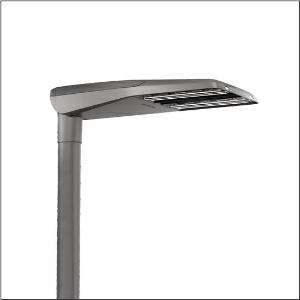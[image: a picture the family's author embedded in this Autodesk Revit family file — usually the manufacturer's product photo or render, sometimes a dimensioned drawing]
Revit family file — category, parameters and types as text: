
# Revit family: streetlight_sl_11_iq_midi___st1_2p1_0_5xc3g41f08me_0c33
name_source: partatom
category: Lighting Fixtures
units: mm (PartAtom-declared; Revit-internal decimal feet)

## family parameters
Cut with Voids When Loaded = No
Host = Face
Light Source = No
Part Type = Normal
Room Calculation Point = No
Round Connector Dimension = Use Diameter
Shared = No

## types (1)
- --- (1 x LED, 18520 lm, 124.7 W, 4000K)
    Apparent Load = 125 VA
    CIE Flux Codes = 31 68 95 100 100
    Color Rendering = 70
    Color Temperature = 4000K
    Default Elevation = 1800 mm
    Description = Streetlight SL 11 iQ midi, mast luminaire, primary light control with 3 zone facetted reflector, of plastic, silver coated, highly specular, primary optical cover: cover, of PMMA, transparent, light distribution: ST1.2P1.0, light emission: direct distribution, primary light characteristic: asymmetric, installation type: post-top, side-entry, LED, High Power LED, rated luminous flux: 18.520lm, luminous efficacy: 149lm/W, light colour: 740, colour temperature: 4000K, control: Street-Remote, optimised constant luminous flux control (CLO 2.0), Auto-Match, Desk-Remote (wireless, voltage-free reading and setting of iQ features in the workshop via application-optimized NFC function/RFID function), Light-Fading, Smart-Wire, Night-Set, Lumen-Switch, Temp-Guard, with cable H07RN-F 5x 1.5mm², mains connection: 230..240V, AC, 50/60Hz, connection cable pre-assembled, cable length: 12,5m, start of lifetime: 125W, end of service life: 132W, reduction: 57W, luminaire housing, of diecast aluminium, powder-coated, Siteco® metallic grey (DB 702S), please order mast flange separately, inclination adjustable without tools: 0°, 5°, 10°, 15° (post-top) | 0°, -5°, -10°, -15° (side-entry), sealing non-destructively replaceable, multi-level sealing system, length: 780mm, width: 376mm, height: 118mm, mast flange for spigot size: 42mm (side-entry): 5XC10008XM4, 60/48mm (side-entry/post-top): 5XC10108XM2, 76/60mm (side-entry/post-top): 5XC10108XM1, equipment: Power, protection rating (complete): IP66, insulation class (complete): insulation class II (safety insulation), certification: CE, ENEC, VDE, impact resistance: IK09, permissible operating ambient temperature for outdoor applications: -25..+50°C, standard-compliant lighting for roads and squares, Environmental Product Declaration (EPD) tested and certified by an independent institute, packaging unit: 1 piece

Light Distribution: ST1.2P1.0
    Height = 118 mm
    Lamp = 1 x LED
    Lamp Light Flux = 18520 lm
    Lamp Power = 124.7 W
    Lamp count = 1
    Length = 780 mm
    Luminous efficacy = 149 lm/W
    Manufacturer = Siteco
    ModVariant = No
    Model = 5XC3G41F08ME
    Number of Poles = 1
    OnlyDefault = Yes
    Power Factor = 1
    Product Name = Streetlight SL 11 iQ midi | ST1.2P1.0
    Product group = mast luminaire | pylon top
    ProductGroupID = 6100
    Protection Class = Protection class II
    Protection Degree = IP 66
    RLX_Detail_Level = 1
    RLX_Emergency_Light_Flux = 0 lm
    RLX_Emergency_Type = 0
    RLX_Emergency_Type_DB = No
    RlxData = <blob elided: 70713 chars, md5=d83bc391>
    Socket = socket
    Standby Power = 0 W
    System Light Flux = 18520 lm
    System Power = 125 W
    Type Comments = factory setting: luminous flux: 100 % | dim-lin: 254 | 557 mA
    Type Image = l_1005960.jpg
    URL = http://relux.com
    VarID = @adj_129573
    Voltage = 0 V
    Weight = 0.00 kg
    Width = 376 mm

## geometry (parser evidence)
native form markers: Blend x4, Sweep x9
no freeform markers — native parametric forms only
